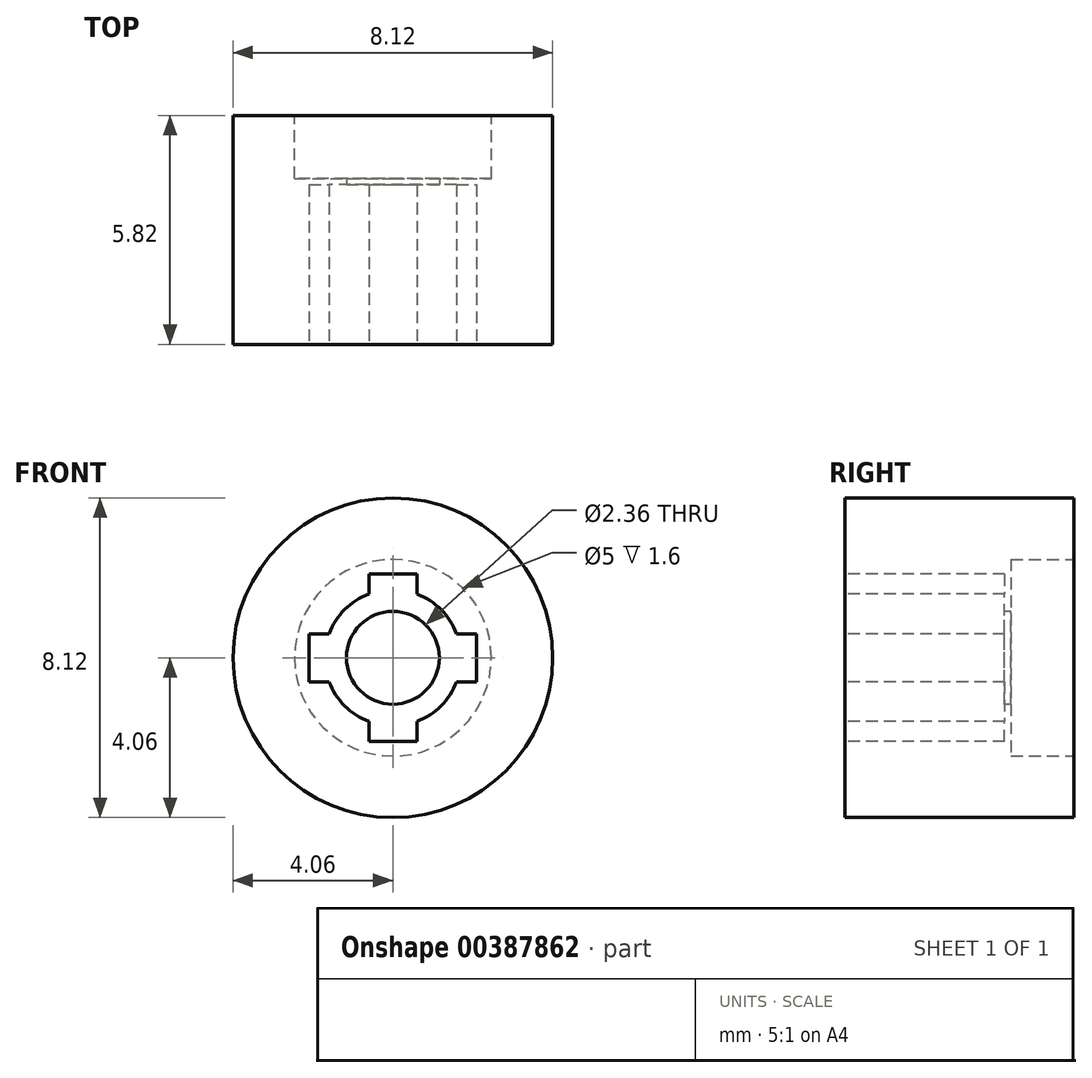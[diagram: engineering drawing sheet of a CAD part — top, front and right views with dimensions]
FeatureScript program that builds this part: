
annotation { "Feature Type Name" : "Feature", "Feature Type Description" : "" }
export const myFeature = defineFeature(function(context is Context, id is Id, definition is map)
    precondition{}
    {
        {
            var Q0;
            Q0=qCreatedBy(makeId("Front.planeOp"),FACE);
            var sketch = newSketch(context, id + "F0", { "sketchPlane" : qUnion([Q0])});
            skCircle(sketch, "E0", {"center": v(0, 0) * mm, "radius": 4.06 * mm});
            skSolve(sketch);
        }
        {
            var Q0;
            Q0=qSketchRegion(id+"F0",true);
            var Q1;
            Q1 = qSketchRegion(id + "F2", true);
            extrude(context, id + "F1", {"entities" : qUnion([Q0, Q1]), "depth" : 5.82 * mm});
        }
        {
            var Q0;
            Q0=makeQuery(id+"F1.opExtrude","CAP_FACE",FACE,{"disambiguationData":[OSD([sQuery(id+"F0.wireOp",EDGE,"E0")])],"isStart":false});
            var sketch = newSketch(context, id + "F2", { "sketchPlane" : qUnion([Q0])});
            skCircle(sketch, "E1", {"center": v(0, 0) * mm, "radius": 1.73 * mm});
            skLineSegment(sketch, "E2", {"start": v(-0.61, 1.62) * mm, "end": v(-0.61, 2.13) * mm});
            skLineSegment(sketch, "E3", {"start": v(-0.61, 2.13) * mm, "end": v(0.61, 2.13) * mm});
            skLineSegment(sketch, "E4", {"start": v(0.61, 2.13) * mm, "end": v(0.61, 1.62) * mm});
            skLineSegment(sketch, "E5.1.0", {"start": v(-2.13, -0.61) * mm, "end": v(-2.13, 0.61) * mm});
            skLineSegment(sketch, "E5.1.1", {"start": v(-1.62, -0.61) * mm, "end": v(-2.13, -0.61) * mm});
            skLineSegment(sketch, "E5.1.2", {"start": v(-2.13, 0.61) * mm, "end": v(-1.62, 0.61) * mm});
            skLineSegment(sketch, "E5.2.0", {"start": v(0.6, -2.13) * mm, "end": v(-0.61, -2.13) * mm});
            skLineSegment(sketch, "E5.2.1", {"start": v(0.61, -1.62) * mm, "end": v(0.6, -2.13) * mm});
            skLineSegment(sketch, "E5.2.2", {"start": v(-0.61, -2.13) * mm, "end": v(-0.61, -1.62) * mm});
            skLineSegment(sketch, "E5.3.0", {"start": v(2.13, 0.6) * mm, "end": v(2.13, -0.61) * mm});
            skLineSegment(sketch, "E5.3.1", {"start": v(1.62, 0.6) * mm, "end": v(2.13, 0.6) * mm});
            skLineSegment(sketch, "E5.3.2", {"start": v(2.13, -0.61) * mm, "end": v(1.62, -0.61) * mm});
            skSolve(sketch);
        }
        {
            var Q0;
            Q0=qSketchRegion(id+"F2",true);
            extrude(context, id + "F3", {"entities" : qUnion([Q0]), "operationType" : NewBodyOperationType.REMOVE, "oppositeDirection" : true, "depth" : 4.06 * mm});
        }
        {
            var Q0;
            Q0=makeQuery(id+"F3.boolean.opBoolean","COPY",FACE,{"derivedFrom":makeQuery(id+"F3.opExtrude","CAP_FACE",FACE,{"disambiguationData":[OSD([sQuery(id+"F2.wireOp",EDGE,"E1"),sQuery(id+"F2.wireOp",EDGE,"E2"),sQuery(id+"F2.wireOp",EDGE,"E3"),sQuery(id+"F2.wireOp",EDGE,"E4"),sQuery(id+"F2.wireOp",EDGE,"E5.1.0"),sQuery(id+"F2.wireOp",EDGE,"E5.1.1"),sQuery(id+"F2.wireOp",EDGE,"E5.1.2"),sQuery(id+"F2.wireOp",EDGE,"E5.2.0"),sQuery(id+"F2.wireOp",EDGE,"E5.2.1"),sQuery(id+"F2.wireOp",EDGE,"E5.2.2"),sQuery(id+"F2.wireOp",EDGE,"E5.3.0"),sQuery(id+"F2.wireOp",EDGE,"E5.3.1"),sQuery(id+"F2.wireOp",EDGE,"E5.3.2")])],"isStart":false})});
            var sketch = newSketch(context, id + "F4", { "sketchPlane" : qUnion([Q0])});
            skCircle(sketch, "E6", {"center": v(0, 0) * mm, "radius": 1.18 * mm});
            skSolve(sketch);
        }
        {
            var Q0;
            Q0=qSketchRegion(id+"F4",true);
            extrude(context, id + "F5", {"entities" : qUnion([Q0]), "operationType" : NewBodyOperationType.REMOVE, "oppositeDirection" : true, "depth" : 25 * mm});
        }
        {
            var Q0;
            Q0=makeQuery(id+"F1.opExtrude","CAP_FACE",FACE,{"disambiguationData":[OSD([sQuery(id+"F0.wireOp",EDGE,"E0")])],"isStart":true});
            var sketch = newSketch(context, id + "F6", { "sketchPlane" : qUnion([Q0])});
            skCircle(sketch, "E7", {"center": v(0, 0) * mm, "radius": 2.5 * mm});
            skSolve(sketch);
        }
        {
            var Q0;
            Q0=makeQuery(id+"F6.imprint","IMPRINT",FACE,{"disambiguationData":[TD([[makeQuery(id+"F6.imprint","IMPRINT",EDGE,{"derivedFrom":sQuery(id+"F6.wireOp",EDGE,"E7")}),1.0]])]});
            extrude(context, id + "F7", {"entities" : qUnion([Q0]), "operationType" : NewBodyOperationType.REMOVE, "oppositeDirection" : true, "depth" : 1.6 * mm});
        }
    });
